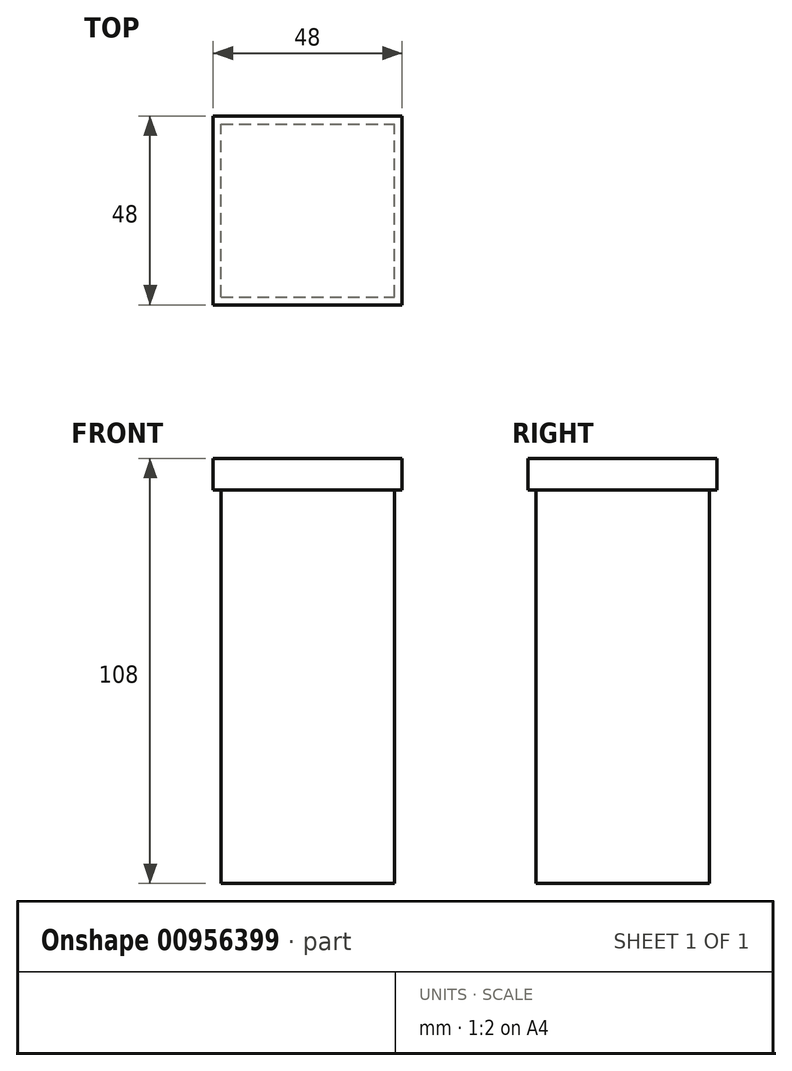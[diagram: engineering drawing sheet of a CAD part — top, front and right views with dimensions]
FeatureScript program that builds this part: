
annotation { "Feature Type Name" : "Feature", "Feature Type Description" : "" }
export const myFeature = defineFeature(function(context is Context, id is Id, definition is map)
    precondition{}
    {
        {
            var Q0;
            Q0=qCreatedBy(makeId("Top.planeOp"),FACE);
            var sketch = newSketch(context, id + "F0", { "sketchPlane" : qUnion([Q0])});
            skLineSegment(sketch, "E0.bottom", {"start": v(0, 0) * mm, "end": v(44, 0) * mm});
            skLineSegment(sketch, "E0.top", {"start": v(0, 44) * mm, "end": v(44, 44) * mm});
            skLineSegment(sketch, "E0.left", {"start": v(0, 0) * mm, "end": v(0, 44) * mm});
            skLineSegment(sketch, "E0.right", {"start": v(44, 0) * mm, "end": v(44, 44) * mm});
            skSolve(sketch);
        }
        {
            var Q0;
            Q0=makeQuery(id+"F0.imprint","IMPRINT",FACE,{"disambiguationData":[TD([[makeQuery(id+"F0.imprint","IMPRINT",EDGE,{"derivedFrom":sQuery(id+"F0.wireOp",EDGE,"E0.bottom")}),1.0]])]});
            extrude(context, id + "F1", {"entities" : qUnion([Q0]), "depth" : 100 * mm, "offsetDistance" : 25 * mm});
        }
        {
            var Q0;
            Q0=makeQuery(id+"F1.opExtrude","CAP_FACE",FACE,{"disambiguationData":[OSD([sQuery(id+"F0.wireOp",EDGE,"E0.bottom"),sQuery(id+"F0.wireOp",EDGE,"E0.top"),sQuery(id+"F0.wireOp",EDGE,"E0.left"),sQuery(id+"F0.wireOp",EDGE,"E0.right")])],"isStart":false});
            var sketch = newSketch(context, id + "F2", { "sketchPlane" : qUnion([Q0])});
            skLineSegment(sketch, "E1", {"start": v(0, 0) * mm, "end": v(0, -2) * mm});
            skLineSegment(sketch, "E2", {"start": v(0, -2) * mm, "end": v(46, -2) * mm});
            skLineSegment(sketch, "E3", {"start": v(46, -2) * mm, "end": v(46, 46) * mm});
            skLineSegment(sketch, "E4", {"start": v(46, 46) * mm, "end": v(-2, 46) * mm});
            skLineSegment(sketch, "E5", {"start": v(-2, 46) * mm, "end": v(-2, -2) * mm});
            skLineSegment(sketch, "E6", {"start": v(-2, -2) * mm, "end": v(46, -2) * mm});
            skSolve(sketch);
        }
        {
            var Q0;
            Q0=makeQuery(id+"F2.imprint","IMPRINT",FACE,{"disambiguationData":[TD([[makeQuery(id+"F2.imprint","IMPRINT",EDGE,{"derivedFrom":sQuery(id+"F2.wireOp",EDGE,"E2")}),1.0]])]});
            var Q1;
            Q1=makeQuery(id+"F2.imprint","IMPRINT",FACE,{"disambiguationData":[TD([[makeQuery(id+"F2.imprint","IMPRINT",EDGE,{"derivedFrom":makeQuery(id+"F1.opExtrude","CAP_EDGE",EDGE,{"disambiguationData":[OSD([sQuery(id+"F0.wireOp",EDGE,"E0.bottom")])],"isStart":false})}),1.0]])]});
            extrude(context, id + "F3", {"entities" : qUnion([Q0, Q1]), "operationType" : NewBodyOperationType.ADD, "depth" : 8 * mm, "offsetDistance" : 25 * mm});
        }
    });
